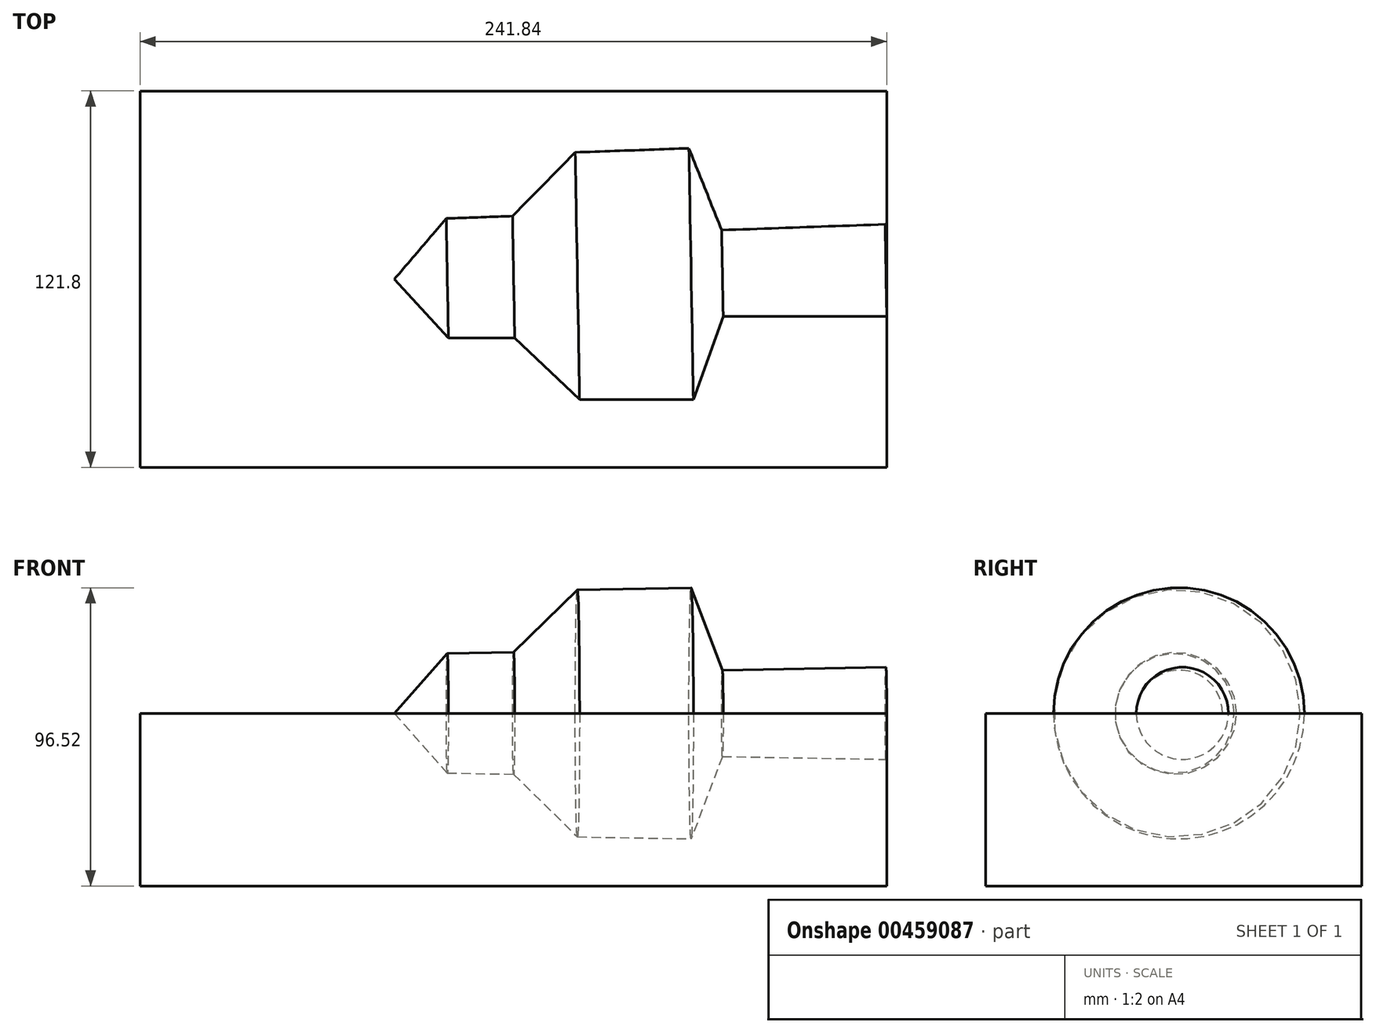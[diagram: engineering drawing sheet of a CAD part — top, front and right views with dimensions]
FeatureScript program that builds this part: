
annotation { "Feature Type Name" : "Feature", "Feature Type Description" : "" }
export const myFeature = defineFeature(function(context is Context, id is Id, definition is map)
    precondition{}
    {
        {
            var Q0;
            Q0=qCreatedBy(makeId("Top.planeOp"),FACE);
            var sketch = newSketch(context, id + "F0", { "sketchPlane" : qUnion([Q0])});
            skLineSegment(sketch, "E0.bottom", {"start": v(-121.35, 58.07) * mm, "end": v(120.5, 58.07) * mm});
            skLineSegment(sketch, "E0.top", {"start": v(-121.35, -63.73) * mm, "end": v(120.5, -63.73) * mm});
            skLineSegment(sketch, "E0.left", {"start": v(-121.35, 58.07) * mm, "end": v(-121.35, -63.73) * mm});
            skLineSegment(sketch, "E0.right", {"start": v(120.5, 58.07) * mm, "end": v(120.5, -63.73) * mm});
            skSolve(sketch);
        }
        {
            var Q0;
            Q0=makeQuery(id+"F0.imprint","IMPRINT",FACE,{"disambiguationData":[TD([[makeQuery(id+"F0.imprint","IMPRINT",EDGE,{"derivedFrom":sQuery(id+"F0.wireOp",EDGE,"E0.bottom")}),-1.0]])]});
            extrude(context, id + "F1", {"entities" : qUnion([Q0]), "depth" : 55.88 * mm});
        }
        {
            var Q0;
            Q0=makeQuery(id+"F1.opExtrude","CAP_FACE",FACE,{"disambiguationData":[OSD([sQuery(id+"F0.wireOp",EDGE,"E0.bottom"),sQuery(id+"F0.wireOp",EDGE,"E0.top"),sQuery(id+"F0.wireOp",EDGE,"E0.left"),sQuery(id+"F0.wireOp",EDGE,"E0.right")])],"isStart":false});
            var sketch = newSketch(context, id + "F2", { "sketchPlane" : qUnion([Q0])});
            skLineSegment(sketch, "E1", {"start": v(120.5, 0) * mm, "end": v(-38.95, -2.83) * mm});
            skPoint(sketch, "E1.startSnap0", {"position": v(120.5, -2.83) * mm});
            skPoint(sketch, "E1.endSnap0", {"position": v(120.5, -2.83) * mm});
            skLineSegment(sketch, "E2", {"start": v(-38.95, -2.83) * mm, "end": v(-21.48, -21.86) * mm});
            skLineSegment(sketch, "E3", {"start": v(-21.48, -21.86) * mm, "end": v(0, -21.86) * mm});
            skLineSegment(sketch, "E4", {"start": v(0, -21.86) * mm, "end": v(21.01, -41.76) * mm});
            skLineSegment(sketch, "E5", {"start": v(21.01, -41.76) * mm, "end": v(57.86, -41.76) * mm});
            skLineSegment(sketch, "E6", {"start": v(57.86, -41.76) * mm, "end": v(67.51, -14.92) * mm});
            skLineSegment(sketch, "E7", {"start": v(67.51, -14.92) * mm, "end": v(120.5, -14.92) * mm});
            skLineSegment(sketch, "E8", {"start": v(120.5, -14.92) * mm, "end": v(120.5, -2.83) * mm});
            skSolve(sketch);
        }
        {
            var Q0;
            {var subQ0=sQuery(id+"F2.wireOp",EDGE,"E1");Q0=makeQuery(id+"F2.imprint","IMPRINT",FACE,{"disambiguationData":[TD([[makeQuery(id+"F2.imprint","IMPRINT",EDGE,{"derivedFrom":subQ0}),1.0]])]});}
            var Q1;
            Q1=sQuery(id+"F2.wireOp",EDGE,"E1");
            revolve(context, id + "F3", {"entities" : qUnion([Q0]), "axis" : qUnion([Q1]), "revolveType" : RevolveType.FULL});
        }
    });
